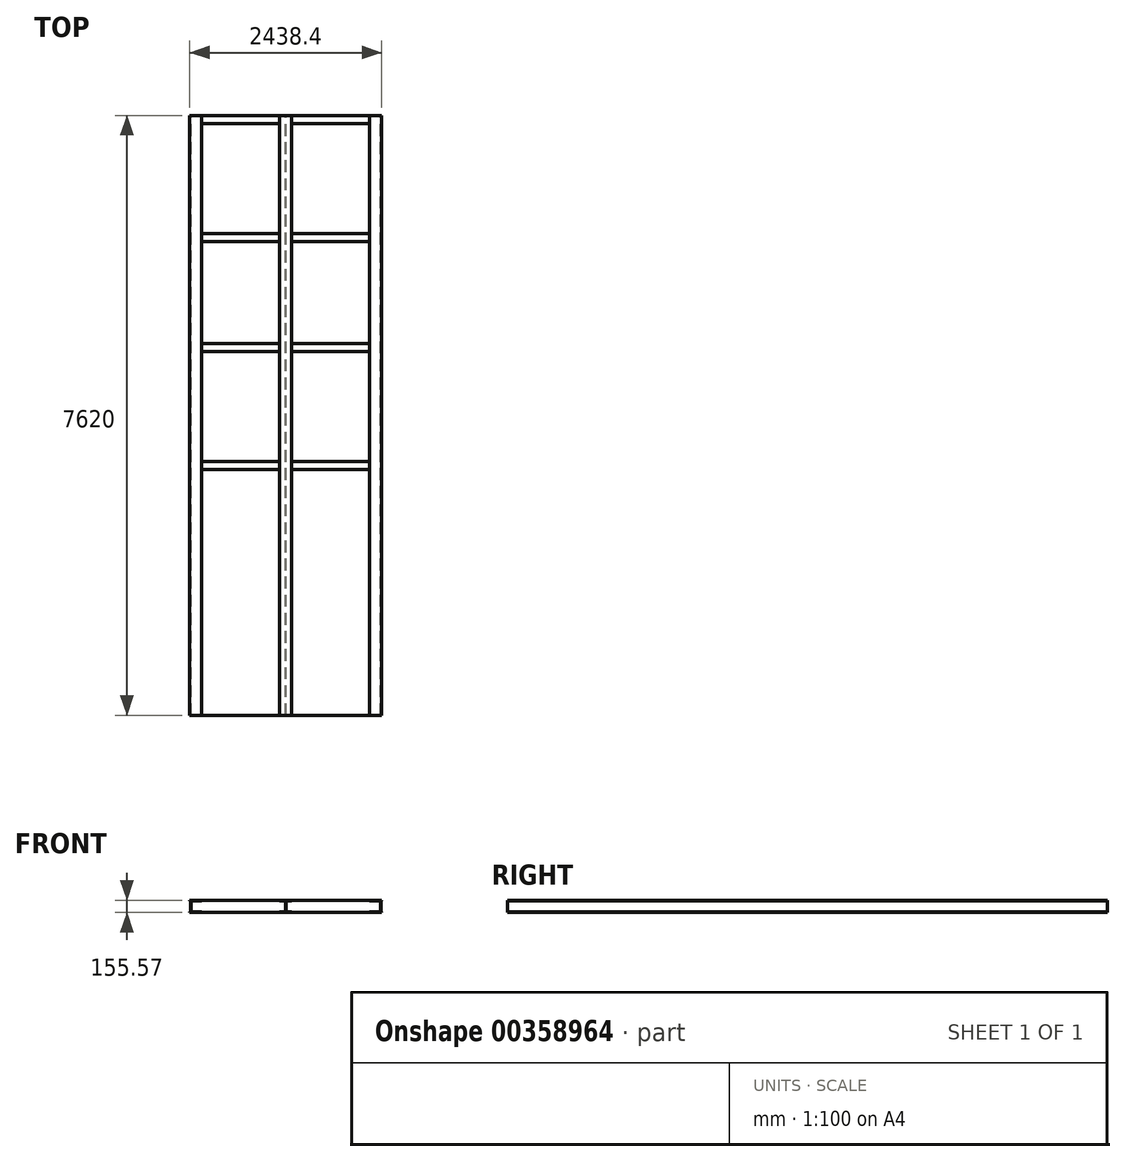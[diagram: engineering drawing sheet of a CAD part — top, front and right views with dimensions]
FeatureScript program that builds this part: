
annotation { "Feature Type Name" : "Feature", "Feature Type Description" : "" }
export const myFeature = defineFeature(function(context is Context, id is Id, definition is map)
    precondition{}
    {
        {
            var Q0;
            Q0=qCreatedBy(makeId("Front.planeOp"),FACE);
            var sketch = newSketch(context, id + "F0", { "sketchPlane" : qUnion([Q0])});
            skLineSegment(sketch, "E0.bottom", {"start": v(0, 0) * mm, "end": v(152.4, 0) * mm});
            skLineSegment(sketch, "E0.top", {"start": v(0, -6.35) * mm, "end": v(152.4, -6.35) * mm});
            skLineSegment(sketch, "E0.left", {"start": v(0, 0) * mm, "end": v(0, -6.35) * mm});
            skLineSegment(sketch, "E0.right", {"start": v(152.4, 0) * mm, "end": v(152.4, -6.35) * mm});
            skLineSegment(sketch, "E1.bottom", {"start": v(0, -149.23) * mm, "end": v(152.4, -149.23) * mm});
            skLineSegment(sketch, "E1.top", {"start": v(0, -155.58) * mm, "end": v(152.4, -155.57) * mm});
            skLineSegment(sketch, "E1.left", {"start": v(0, -149.23) * mm, "end": v(0, -155.58) * mm});
            skLineSegment(sketch, "E1.right", {"start": v(152.4, -149.22) * mm, "end": v(152.4, -155.57) * mm});
            skLineSegment(sketch, "E2.bottom", {"start": v(144.46, -6.35) * mm, "end": v(138.11, -6.35) * mm});
            skLineSegment(sketch, "E2.top", {"start": v(144.46, -149.23) * mm, "end": v(138.11, -149.23) * mm});
            skLineSegment(sketch, "E2.left", {"start": v(144.46, -6.35) * mm, "end": v(144.46, -149.23) * mm});
            skLineSegment(sketch, "E2.right", {"start": v(138.11, -6.35) * mm, "end": v(138.11, -149.23) * mm});
            skSolve(sketch);
        }
        {
            var Q0;
            Q0 = qSketchRegion(id + "F0", true);
            extrude(context, id + "F1", {"entities" : qUnion([Q0]), "depth" : 7620 * mm});
        }
        {
            var Q0;
            Q0=qCreatedBy(makeId("Front.planeOp"),FACE);
            var sketch = newSketch(context, id + "F2", { "sketchPlane" : qUnion([Q0])});
            skLineSegment(sketch, "E3.bottom", {"start": v(-2286, 0) * mm, "end": v(-2133.6, 0) * mm});
            skLineSegment(sketch, "E3.top", {"start": v(-2286, -6.35) * mm, "end": v(-2133.6, -6.35) * mm});
            skLineSegment(sketch, "E3.left", {"start": v(-2286, 0) * mm, "end": v(-2286, -6.35) * mm});
            skLineSegment(sketch, "E3.right", {"start": v(-2133.6, 0) * mm, "end": v(-2133.6, -6.35) * mm});
            skLineSegment(sketch, "E4.bottom", {"start": v(-2286, -149.23) * mm, "end": v(-2133.6, -149.23) * mm});
            skLineSegment(sketch, "E4.top", {"start": v(-2286, -155.58) * mm, "end": v(-2133.6, -155.58) * mm});
            skLineSegment(sketch, "E4.left", {"start": v(-2286, -149.23) * mm, "end": v(-2286, -155.58) * mm});
            skLineSegment(sketch, "E4.right", {"start": v(-2133.6, -149.23) * mm, "end": v(-2133.6, -155.58) * mm});
            skLineSegment(sketch, "E5.bottom", {"start": v(-2278.06, -6.35) * mm, "end": v(-2271.71, -6.35) * mm});
            skLineSegment(sketch, "E5.top", {"start": v(-2278.06, -149.23) * mm, "end": v(-2271.71, -149.23) * mm});
            skLineSegment(sketch, "E5.left", {"start": v(-2278.06, -6.35) * mm, "end": v(-2278.06, -149.23) * mm});
            skLineSegment(sketch, "E5.right", {"start": v(-2271.71, -6.35) * mm, "end": v(-2271.71, -149.23) * mm});
            skSolve(sketch);
        }
        {
            var Q0;
            Q0 = qSketchRegion(id + "F2", true);
            extrude(context, id + "F3", {"entities" : qUnion([Q0]), "depth" : 7620 * mm});
        }
        {
            var Q0;
            Q0=qCreatedBy(makeId("Front.planeOp"),FACE);
            var sketch = newSketch(context, id + "F4", { "sketchPlane" : qUnion([Q0])});
            skLineSegment(sketch, "E6.0", {"start": v(-2286, 0) * mm, "end": v(-2133.6, 0) * mm});
            skPoint(sketch, "E7.0", {"position": v(-2286, -3.18) * mm});
            skLineSegment(sketch, "E8.0", {"start": v(-2286, 0) * mm, "end": v(-2286, -6.35) * mm});
            skLineSegment(sketch, "E9.0.0", {"start": v(-2286, -6.35) * mm, "end": v(-2278.06, -6.35) * mm, "construction": true});
            skLineSegment(sketch, "E9.0.1", {"start": v(-2278.06, -6.35) * mm, "end": v(-2278.06, -149.23) * mm, "construction": true});
            skLineSegment(sketch, "E9.0.2", {"start": v(-2278.06, -149.23) * mm, "end": v(-2286, -149.23) * mm, "construction": true});
            skLineSegment(sketch, "E9.0.3", {"start": v(-2286, -149.23) * mm, "end": v(-2286, -155.58) * mm, "construction": true});
            skLineSegment(sketch, "E9.0.4", {"start": v(-2286, -155.58) * mm, "end": v(-2133.6, -155.58) * mm, "construction": true});
            skLineSegment(sketch, "E9.0.5", {"start": v(-2133.6, -155.58) * mm, "end": v(-2133.6, -149.23) * mm, "construction": true});
            skLineSegment(sketch, "E9.0.6", {"start": v(-2133.6, -149.23) * mm, "end": v(-2271.71, -149.23) * mm, "construction": true});
            skLineSegment(sketch, "E9.0.7", {"start": v(-2271.71, -149.23) * mm, "end": v(-2271.71, -6.35) * mm, "construction": true});
            skLineSegment(sketch, "E9.0.8", {"start": v(-2271.71, -6.35) * mm, "end": v(-2133.6, -6.35) * mm, "construction": true});
            skLineSegment(sketch, "E9.0.9", {"start": v(-2133.6, -6.35) * mm, "end": v(-2133.6, 0) * mm, "construction": true});
            skLineSegment(sketch, "E9.0.10", {"start": v(-2133.6, 0) * mm, "end": v(-2286, 0) * mm, "construction": true});
            skLineSegment(sketch, "E9.0.11", {"start": v(-2286, 0) * mm, "end": v(-2286, -6.35) * mm, "construction": true});
            skLineSegment(sketch, "E10.0", {"start": v(0, 0) * mm, "end": v(152.4, 0) * mm, "construction": true});
            skLineSegment(sketch, "E11.0", {"start": v(0, -6.35) * mm, "end": v(138.11, -6.35) * mm, "construction": true});
            skLineSegment(sketch, "E12.0", {"start": v(144.46, -6.35) * mm, "end": v(144.46, -149.23) * mm, "construction": true});
            skLineSegment(sketch, "E13.0", {"start": v(138.11, -6.35) * mm, "end": v(138.11, -149.23) * mm, "construction": true});
            skLineSegment(sketch, "E14.0", {"start": v(0, -149.23) * mm, "end": v(138.11, -149.23) * mm, "construction": true});
            skPoint(sketch, "E15.0", {"position": v(0, -152.4) * mm});
            skLineSegment(sketch, "E16", {"start": v(152.4, 0) * mm, "end": v(-2286, 0) * mm, "construction": true});
            skLineSegment(sketch, "E17", {"start": v(-1066.8, 457.17) * mm, "end": v(-1066.8, -578.58) * mm, "construction": true});
            skLineSegment(sketch, "E18.bottom", {"start": v(-1143, 0) * mm, "end": v(-990.6, 0) * mm});
            skLineSegment(sketch, "E18.top", {"start": v(-1143, -6.35) * mm, "end": v(-990.6, -6.35) * mm});
            skLineSegment(sketch, "E18.left", {"start": v(-1143, 0) * mm, "end": v(-1143, -6.35) * mm});
            skLineSegment(sketch, "E18.right", {"start": v(-990.6, 0) * mm, "end": v(-990.6, -6.35) * mm});
            skLineSegment(sketch, "E19.bottom", {"start": v(-1143, -149.23) * mm, "end": v(-990.6, -149.23) * mm});
            skLineSegment(sketch, "E19.top", {"start": v(-1143, -155.58) * mm, "end": v(-990.6, -155.58) * mm});
            skLineSegment(sketch, "E19.left", {"start": v(-1143, -149.23) * mm, "end": v(-1143, -155.58) * mm});
            skLineSegment(sketch, "E19.right", {"start": v(-990.6, -149.23) * mm, "end": v(-990.6, -155.58) * mm});
            skLineSegment(sketch, "E20.bottom", {"start": v(-1069.97, -6.35) * mm, "end": v(-1063.62, -6.35) * mm});
            skLineSegment(sketch, "E20.top", {"start": v(-1069.97, -149.23) * mm, "end": v(-1063.62, -149.23) * mm});
            skLineSegment(sketch, "E20.left", {"start": v(-1069.97, -6.35) * mm, "end": v(-1069.97, -149.23) * mm});
            skLineSegment(sketch, "E20.right", {"start": v(-1063.62, -6.35) * mm, "end": v(-1063.62, -149.23) * mm});
            skSolve(sketch);
        }
        {
            var Q0;
            Q0 = qSketchRegion(id + "F4", true);
            extrude(context, id + "F5", {"entities" : qUnion([Q0]), "depth" : 7620 * mm});
        }
        {
            var Q0;
            Q0=qCreatedBy(makeId("Front.planeOp"),FACE);
            var sketch = newSketch(context, id + "F6", { "sketchPlane" : qUnion([Q0])});
            skLineSegment(sketch, "E21.0", {"start": v(-2286, 0) * mm, "end": v(-2133.6, 0) * mm, "construction": true});
            skLineSegment(sketch, "E22.0", {"start": v(-2133.6, 0) * mm, "end": v(-2133.6, -6.35) * mm, "construction": true});
            skLineSegment(sketch, "E23.0", {"start": v(-2271.71, -6.35) * mm, "end": v(-2133.6, -6.35) * mm, "construction": true});
            skLineSegment(sketch, "E24.0", {"start": v(-2271.71, -6.35) * mm, "end": v(-2271.71, -149.23) * mm, "construction": true});
            skLineSegment(sketch, "E25.0", {"start": v(-2278.06, -6.35) * mm, "end": v(-2278.06, -149.23) * mm, "construction": true});
            skLineSegment(sketch, "E26.0", {"start": v(-2286, -6.35) * mm, "end": v(-2278.06, -6.35) * mm, "construction": true});
            skPoint(sketch, "E27.0", {"position": v(-2286, -3.18) * mm});
            skLineSegment(sketch, "E28.0", {"start": v(-2286, 0) * mm, "end": v(-2286, -6.35) * mm, "construction": true});
            skLineSegment(sketch, "E29.0", {"start": v(-2271.71, -149.23) * mm, "end": v(-2133.6, -149.23) * mm, "construction": true});
            skLineSegment(sketch, "E30.0", {"start": v(-2133.6, -149.23) * mm, "end": v(-2133.6, -155.58) * mm, "construction": true});
            skLineSegment(sketch, "E31.0", {"start": v(-2286, -155.58) * mm, "end": v(-2133.6, -155.58) * mm, "construction": true});
            skPoint(sketch, "E32.0", {"position": v(-2286, -152.4) * mm});
            skLineSegment(sketch, "E33.0", {"start": v(-2286, -149.23) * mm, "end": v(-2278.06, -149.23) * mm, "construction": true});
            skLineSegment(sketch, "E34.0", {"start": v(-2286, -149.23) * mm, "end": v(-2286, -155.58) * mm, "construction": true});
            skLineSegment(sketch, "E35.0", {"start": v(-1143, 0) * mm, "end": v(-990.6, 0) * mm, "construction": true});
            skPoint(sketch, "E36.0", {"position": v(-1143, -3.18) * mm});
            skLineSegment(sketch, "E37.0", {"start": v(-1143, -6.35) * mm, "end": v(-1069.97, -6.35) * mm, "construction": true});
            skLineSegment(sketch, "E38.0", {"start": v(-1143, 0) * mm, "end": v(-1143, -6.35) * mm, "construction": true});
            skLineSegment(sketch, "E39.0", {"start": v(-1069.97, -6.35) * mm, "end": v(-1069.97, -149.23) * mm, "construction": true});
            skLineSegment(sketch, "E40.0", {"start": v(-1143, -149.23) * mm, "end": v(-1069.97, -149.23) * mm, "construction": true});
            skLineSegment(sketch, "E41.0", {"start": v(-1143, -149.23) * mm, "end": v(-1143, -155.58) * mm, "construction": true});
            skLineSegment(sketch, "E42.0", {"start": v(-990.6, -149.23) * mm, "end": v(-990.6, -155.58) * mm, "construction": true});
            skLineSegment(sketch, "E43.0", {"start": v(-1063.62, -149.23) * mm, "end": v(-990.6, -149.23) * mm, "construction": true});
            skLineSegment(sketch, "E44.0", {"start": v(-1063.62, -6.35) * mm, "end": v(-1063.62, -149.23) * mm, "construction": true});
            skLineSegment(sketch, "E45.0", {"start": v(-1063.62, -6.35) * mm, "end": v(-990.6, -6.35) * mm, "construction": true});
            skLineSegment(sketch, "E46.0", {"start": v(-990.6, 0) * mm, "end": v(-990.6, -6.35) * mm, "construction": true});
            skLineSegment(sketch, "E47.0", {"start": v(0, 0) * mm, "end": v(152.4, 0) * mm, "construction": true});
            skLineSegment(sketch, "E48.0", {"start": v(0, 0) * mm, "end": v(0, -6.35) * mm, "construction": true});
            skLineSegment(sketch, "E49.0", {"start": v(0, -6.35) * mm, "end": v(138.11, -6.35) * mm, "construction": true});
            skLineSegment(sketch, "E50.0", {"start": v(138.11, -6.35) * mm, "end": v(138.11, -149.23) * mm, "construction": true});
            skLineSegment(sketch, "E51.0", {"start": v(0, -149.23) * mm, "end": v(138.11, -149.23) * mm, "construction": true});
            skLineSegment(sketch, "E52.0", {"start": v(0, -149.23) * mm, "end": v(0, -155.58) * mm, "construction": true});
            skLineSegment(sketch, "E53.0", {"start": v(0, -155.58) * mm, "end": v(152.4, -155.57) * mm, "construction": true});
            skLineSegment(sketch, "E54", {"start": v(0, 0) * mm, "end": v(0, -6.35) * mm});
            skLineSegment(sketch, "E55", {"start": v(0, -6.35) * mm, "end": v(138.11, -6.35) * mm});
            skLineSegment(sketch, "E56", {"start": v(138.11, -6.35) * mm, "end": v(138.11, -149.23) * mm});
            skLineSegment(sketch, "E57", {"start": v(138.11, -149.23) * mm, "end": v(0, -149.23) * mm});
            skLineSegment(sketch, "E58", {"start": v(0, -149.23) * mm, "end": v(0, -155.58) * mm});
            skLineSegment(sketch, "E59", {"start": v(0, -155.58) * mm, "end": v(-990.6, -155.58) * mm});
            skLineSegment(sketch, "E60", {"start": v(-990.6, -149.23) * mm, "end": v(-1063.62, -149.23) * mm});
            skLineSegment(sketch, "E61", {"start": v(-990.6, -155.58) * mm, "end": v(-990.6, -149.23) * mm});
            skLineSegment(sketch, "E62", {"start": v(-1063.62, -149.23) * mm, "end": v(-1063.62, -6.35) * mm});
            skLineSegment(sketch, "E63", {"start": v(-1063.62, -6.35) * mm, "end": v(-990.6, -6.35) * mm});
            skLineSegment(sketch, "E64", {"start": v(-990.6, -6.35) * mm, "end": v(-990.6, 0) * mm});
            skLineSegment(sketch, "E65", {"start": v(-990.6, 0) * mm, "end": v(0, 0) * mm});
            skLineSegment(sketch, "E66", {"start": v(-1143, 0) * mm, "end": v(-1143, -6.35) * mm});
            skLineSegment(sketch, "E67", {"start": v(-1143, -6.35) * mm, "end": v(-1069.97, -6.35) * mm});
            skLineSegment(sketch, "E68", {"start": v(-1069.97, -6.35) * mm, "end": v(-1069.97, -149.23) * mm});
            skLineSegment(sketch, "E69", {"start": v(-1069.97, -149.23) * mm, "end": v(-1143, -149.23) * mm});
            skLineSegment(sketch, "E70", {"start": v(-1143, -149.23) * mm, "end": v(-1143, -155.58) * mm});
            skLineSegment(sketch, "E71", {"start": v(-1143, -155.58) * mm, "end": v(-2133.6, -155.58) * mm});
            skLineSegment(sketch, "E72", {"start": v(-2133.6, -155.58) * mm, "end": v(-2133.6, -149.23) * mm});
            skLineSegment(sketch, "E73", {"start": v(-2133.6, -149.23) * mm, "end": v(-2271.71, -149.23) * mm});
            skLineSegment(sketch, "E74", {"start": v(-2271.71, -149.23) * mm, "end": v(-2271.71, -6.35) * mm});
            skLineSegment(sketch, "E75", {"start": v(-2271.71, -6.35) * mm, "end": v(-2133.6, -6.35) * mm});
            skLineSegment(sketch, "E76", {"start": v(-2133.6, -6.35) * mm, "end": v(-2133.6, 0) * mm});
            skLineSegment(sketch, "E77", {"start": v(-2133.6, 0) * mm, "end": v(-1143, 0) * mm});
            skSolve(sketch);
        }
        {
            var Q0;
            Q0 = qSketchRegion(id + "F6", true);
            extrude(context, id + "F7", {"entities" : qUnion([Q0]), "depth" : 7620 * mm});
        }
        {
            var Q0;
            Q0=makeQuery(id+"F7.opExtrude","SWEPT_FACE",FACE,{"disambiguationData":[OSD([sQuery(id+"F6.wireOp",EDGE,"E65")])]});
            var sketch = newSketch(context, id + "F8", { "sketchPlane" : qUnion([Q0])});
            skLineSegment(sketch, "E78", {"start": v(-990.6, -1498.6) * mm, "end": v(0, -1498.6) * mm, "construction": true});
            skLineSegment(sketch, "E79.bottom", {"start": v(-990.6, -1498.6) * mm, "end": v(0, -1498.6) * mm});
            skLineSegment(sketch, "E79.top", {"start": v(-990.6, -1600.2) * mm, "end": v(0, -1600.2) * mm});
            skLineSegment(sketch, "E79.left", {"start": v(-990.6, -1498.6) * mm, "end": v(-990.6, -1600.2) * mm});
            skLineSegment(sketch, "E79.right", {"start": v(0, -1498.6) * mm, "end": v(0, -1600.2) * mm});
            skLineSegment(sketch, "E80.0", {"start": v(-1143, -7620) * mm, "end": v(-1143, 0) * mm, "construction": true});
            skLineSegment(sketch, "E81.0", {"start": v(-2133.6, -7620) * mm, "end": v(-2133.6, 0) * mm, "construction": true});
            skLineSegment(sketch, "E82.0", {"start": v(-990.6, -7620) * mm, "end": v(-990.6, 0) * mm, "construction": true});
            skLineSegment(sketch, "E83.0", {"start": v(0, -7620) * mm, "end": v(0, 0) * mm, "construction": true});
            skLineSegment(sketch, "E84", {"start": v(-1143, -1498.6) * mm, "end": v(-2133.6, -1498.6) * mm, "construction": true});
            skLineSegment(sketch, "E85.bottom", {"start": v(-2133.6, -1498.6) * mm, "end": v(-1143, -1498.6) * mm});
            skLineSegment(sketch, "E85.top", {"start": v(-2133.6, -1600.2) * mm, "end": v(-1143, -1600.2) * mm});
            skLineSegment(sketch, "E85.left", {"start": v(-2133.6, -1498.6) * mm, "end": v(-2133.6, -1600.2) * mm});
            skLineSegment(sketch, "E85.right", {"start": v(-1143, -1498.6) * mm, "end": v(-1143, -1600.2) * mm});
            skLineSegment(sketch, "E86.bottom", {"start": v(-2133.6, 0) * mm, "end": v(-1143, 0) * mm});
            skLineSegment(sketch, "E86.top", {"start": v(-2133.6, -101.6) * mm, "end": v(-1143, -101.6) * mm});
            skLineSegment(sketch, "E86.left", {"start": v(-2133.6, 0) * mm, "end": v(-2133.6, -101.6) * mm});
            skLineSegment(sketch, "E86.right", {"start": v(-1143, 0) * mm, "end": v(-1143, -101.6) * mm});
            skLineSegment(sketch, "E87.bottom", {"start": v(-990.6, 0) * mm, "end": v(0, 0) * mm});
            skLineSegment(sketch, "E87.top", {"start": v(-990.6, -101.6) * mm, "end": v(0, -101.6) * mm});
            skLineSegment(sketch, "E87.left", {"start": v(-990.6, 0) * mm, "end": v(-990.6, -101.6) * mm});
            skLineSegment(sketch, "E87.right", {"start": v(0, 0) * mm, "end": v(0, -101.6) * mm});
            skLineSegment(sketch, "E88", {"start": v(-2133.6, -2997.2) * mm, "end": v(0, -2997.2) * mm, "construction": true});
            skLineSegment(sketch, "E89", {"start": v(-2133.6, -4495.8) * mm, "end": v(0, -4495.8) * mm, "construction": true});
            skLineSegment(sketch, "E90.bottom", {"start": v(0, -2997.2) * mm, "end": v(-990.6, -2997.2) * mm});
            skLineSegment(sketch, "E90.top", {"start": v(0, -2895.6) * mm, "end": v(-990.6, -2895.6) * mm});
            skLineSegment(sketch, "E90.left", {"start": v(0, -2997.2) * mm, "end": v(0, -2895.6) * mm});
            skLineSegment(sketch, "E90.right", {"start": v(-990.6, -2997.2) * mm, "end": v(-990.6, -2895.6) * mm});
            skLineSegment(sketch, "E91.bottom", {"start": v(-1143, -2997.2) * mm, "end": v(-2133.6, -2997.2) * mm});
            skLineSegment(sketch, "E91.top", {"start": v(-1143, -2895.6) * mm, "end": v(-2133.6, -2895.6) * mm});
            skLineSegment(sketch, "E91.left", {"start": v(-1143, -2997.2) * mm, "end": v(-1143, -2895.6) * mm});
            skLineSegment(sketch, "E91.right", {"start": v(-2133.6, -2997.2) * mm, "end": v(-2133.6, -2895.6) * mm});
            skLineSegment(sketch, "E92.bottom", {"start": v(0, -4495.8) * mm, "end": v(-990.6, -4495.8) * mm});
            skLineSegment(sketch, "E92.top", {"start": v(0, -4394.2) * mm, "end": v(-990.6, -4394.2) * mm});
            skLineSegment(sketch, "E92.left", {"start": v(0, -4495.8) * mm, "end": v(0, -4394.2) * mm});
            skLineSegment(sketch, "E92.right", {"start": v(-990.6, -4495.8) * mm, "end": v(-990.6, -4394.2) * mm});
            skLineSegment(sketch, "E93.bottom", {"start": v(-2133.6, -4495.8) * mm, "end": v(-1143, -4495.8) * mm});
            skLineSegment(sketch, "E93.top", {"start": v(-2133.6, -4394.2) * mm, "end": v(-1143, -4394.2) * mm});
            skLineSegment(sketch, "E93.left", {"start": v(-2133.6, -4495.8) * mm, "end": v(-2133.6, -4394.2) * mm});
            skLineSegment(sketch, "E93.right", {"start": v(-1143, -4495.8) * mm, "end": v(-1143, -4394.2) * mm});
            skSolve(sketch);
        }
        {
            var Q0;
            Q0 = qSketchRegion(id + "F8", true);
            extrude(context, id + "F9", {"entities" : qUnion([Q0]), "oppositeDirection" : true, "depth" : 6.35 * mm});
        }
    });
